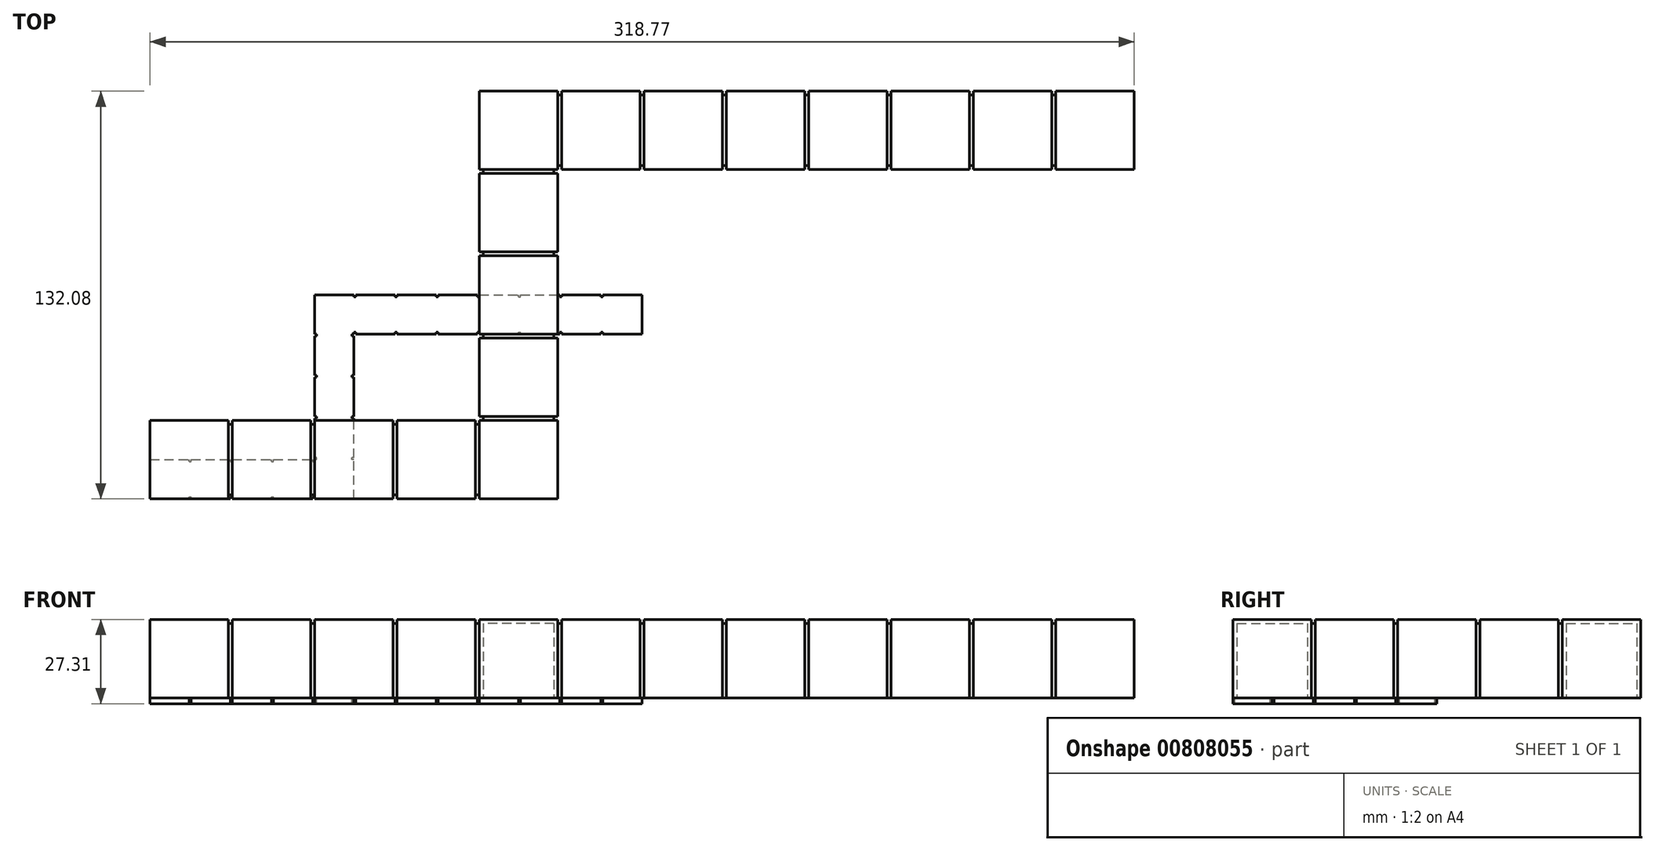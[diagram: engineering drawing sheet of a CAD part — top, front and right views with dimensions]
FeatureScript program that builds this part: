
annotation { "Feature Type Name" : "Feature", "Feature Type Description" : "" }
export const myFeature = defineFeature(function(context is Context, id is Id, definition is map)
    precondition{}
    {
        {
            var Q0;
            Q0=qCreatedBy(makeId("Top.planeOp"),FACE);
            var sketch = newSketch(context, id + "F0", { "sketchPlane" : qUnion([Q0])});
            skLineSegment(sketch, "E0.bottom", {"start": v(0, 0) * mm, "end": v(25.4, 0) * mm});
            skLineSegment(sketch, "E0.top", {"start": v(0, 25.4) * mm, "end": v(25.4, 25.4) * mm});
            skLineSegment(sketch, "E0.left", {"start": v(0, 0) * mm, "end": v(0, 25.4) * mm});
            skLineSegment(sketch, "E0.right", {"start": v(25.4, 0) * mm, "end": v(25.4, 25.4) * mm});
            skLineSegment(sketch, "E1.bottom", {"start": v(25.4, 24.13) * mm, "end": v(26.67, 24.13) * mm});
            skLineSegment(sketch, "E1.top", {"start": v(25.4, 1.27) * mm, "end": v(26.67, 1.27) * mm});
            skLineSegment(sketch, "E1.left", {"start": v(25.4, 24.13) * mm, "end": v(25.4, 1.27) * mm});
            skLineSegment(sketch, "E1.right", {"start": v(26.67, 24.13) * mm, "end": v(26.67, 1.27) * mm});
            skLineSegment(sketch, "E2", {"start": v(25.4, 25.4) * mm, "end": v(25.4, 24.13) * mm});
            skLineSegment(sketch, "E3", {"start": v(25.4, 0) * mm, "end": v(25.4, 1.27) * mm});
            skLineSegment(sketch, "E4.bottom", {"start": v(26.67, 0) * mm, "end": v(52.07, 0) * mm});
            skLineSegment(sketch, "E4.top", {"start": v(26.67, 25.4) * mm, "end": v(52.07, 25.4) * mm});
            skLineSegment(sketch, "E4.left", {"start": v(26.67, 0) * mm, "end": v(26.67, 25.4) * mm});
            skLineSegment(sketch, "E4.right", {"start": v(52.07, 0) * mm, "end": v(52.07, 25.4) * mm});
            skLineSegment(sketch, "E5.bottom", {"start": v(52.07, 24.13) * mm, "end": v(53.34, 24.13) * mm});
            skLineSegment(sketch, "E5.top", {"start": v(52.07, 1.27) * mm, "end": v(53.34, 1.27) * mm});
            skLineSegment(sketch, "E5.left", {"start": v(52.07, 24.13) * mm, "end": v(52.07, 1.27) * mm});
            skLineSegment(sketch, "E5.right", {"start": v(53.34, 24.13) * mm, "end": v(53.34, 1.27) * mm});
            skLineSegment(sketch, "E6", {"start": v(52.07, 25.4) * mm, "end": v(52.07, 24.13) * mm});
            skLineSegment(sketch, "E7", {"start": v(52.07, 0) * mm, "end": v(52.07, 1.27) * mm});
            skLineSegment(sketch, "E8.bottom", {"start": v(53.34, 0) * mm, "end": v(78.74, 0) * mm});
            skLineSegment(sketch, "E8.top", {"start": v(53.34, 25.4) * mm, "end": v(78.74, 25.4) * mm});
            skLineSegment(sketch, "E8.left", {"start": v(53.34, 0) * mm, "end": v(53.34, 25.4) * mm});
            skLineSegment(sketch, "E8.right", {"start": v(78.74, 0) * mm, "end": v(78.74, 25.4) * mm});
            skLineSegment(sketch, "E9.bottom", {"start": v(78.74, 24.13) * mm, "end": v(80, 24.13) * mm});
            skLineSegment(sketch, "E9.top", {"start": v(78.74, 1.27) * mm, "end": v(80, 1.27) * mm});
            skLineSegment(sketch, "E9.left", {"start": v(78.74, 24.13) * mm, "end": v(78.74, 1.27) * mm});
            skLineSegment(sketch, "E9.right", {"start": v(80, 24.13) * mm, "end": v(80, 1.27) * mm});
            skLineSegment(sketch, "E10", {"start": v(78.74, 25.4) * mm, "end": v(78.74, 24.13) * mm});
            skLineSegment(sketch, "E11", {"start": v(78.74, 0) * mm, "end": v(78.74, 1.27) * mm});
            skLineSegment(sketch, "E12.bottom", {"start": v(80, 0) * mm, "end": v(105.4, 0) * mm});
            skLineSegment(sketch, "E12.top", {"start": v(80, 25.4) * mm, "end": v(105.4, 25.4) * mm});
            skLineSegment(sketch, "E12.left", {"start": v(80, 0) * mm, "end": v(80, 25.4) * mm});
            skLineSegment(sketch, "E12.right", {"start": v(105.4, 0) * mm, "end": v(105.4, 25.4) * mm});
            skLineSegment(sketch, "E13.bottom", {"start": v(105.4, 24.13) * mm, "end": v(106.68, 24.13) * mm});
            skLineSegment(sketch, "E13.top", {"start": v(105.4, 1.27) * mm, "end": v(106.68, 1.27) * mm});
            skLineSegment(sketch, "E13.left", {"start": v(105.4, 24.13) * mm, "end": v(105.4, 1.27) * mm});
            skLineSegment(sketch, "E13.right", {"start": v(106.68, 24.13) * mm, "end": v(106.68, 1.27) * mm});
            skLineSegment(sketch, "E14", {"start": v(105.4, 25.4) * mm, "end": v(105.4, 24.13) * mm});
            skLineSegment(sketch, "E15", {"start": v(105.4, 0) * mm, "end": v(105.4, 1.27) * mm});
            skLineSegment(sketch, "E16.bottom", {"start": v(132.08, 0) * mm, "end": v(132.08, 25.4) * mm});
            skLineSegment(sketch, "E16.top", {"start": v(106.68, 0) * mm, "end": v(106.68, 25.4) * mm});
            skLineSegment(sketch, "E16.left", {"start": v(132.08, 0) * mm, "end": v(106.68, 0) * mm});
            skLineSegment(sketch, "E16.right", {"start": v(132.08, 25.4) * mm, "end": v(106.68, 25.4) * mm});
            skLineSegment(sketch, "E17.bottom", {"start": v(107.95, 25.4) * mm, "end": v(107.95, 26.67) * mm});
            skLineSegment(sketch, "E17.top", {"start": v(130.8, 25.4) * mm, "end": v(130.8, 26.67) * mm});
            skLineSegment(sketch, "E17.left", {"start": v(107.95, 25.4) * mm, "end": v(130.8, 25.4) * mm});
            skLineSegment(sketch, "E17.right", {"start": v(107.95, 26.67) * mm, "end": v(130.8, 26.67) * mm});
            skLineSegment(sketch, "E18", {"start": v(106.68, 25.4) * mm, "end": v(107.95, 25.4) * mm});
            skLineSegment(sketch, "E19", {"start": v(132.08, 25.4) * mm, "end": v(130.8, 25.4) * mm});
            skLineSegment(sketch, "E20.bottom", {"start": v(132.08, 26.67) * mm, "end": v(132.08, 52.07) * mm});
            skLineSegment(sketch, "E20.top", {"start": v(106.68, 26.67) * mm, "end": v(106.68, 52.07) * mm});
            skLineSegment(sketch, "E20.left", {"start": v(132.08, 26.67) * mm, "end": v(106.68, 26.67) * mm});
            skLineSegment(sketch, "E20.right", {"start": v(132.08, 52.07) * mm, "end": v(106.68, 52.07) * mm});
            skLineSegment(sketch, "E21.bottom", {"start": v(107.95, 52.07) * mm, "end": v(107.95, 53.34) * mm});
            skLineSegment(sketch, "E21.top", {"start": v(130.8, 52.07) * mm, "end": v(130.8, 53.34) * mm});
            skLineSegment(sketch, "E21.left", {"start": v(107.95, 52.07) * mm, "end": v(130.8, 52.07) * mm});
            skLineSegment(sketch, "E21.right", {"start": v(107.95, 53.34) * mm, "end": v(130.8, 53.34) * mm});
            skLineSegment(sketch, "E22", {"start": v(106.68, 52.07) * mm, "end": v(107.95, 52.07) * mm});
            skLineSegment(sketch, "E23", {"start": v(132.08, 52.07) * mm, "end": v(130.8, 52.07) * mm});
            skLineSegment(sketch, "E24.bottom", {"start": v(132.08, 53.34) * mm, "end": v(132.08, 78.74) * mm});
            skLineSegment(sketch, "E24.top", {"start": v(106.68, 53.34) * mm, "end": v(106.68, 78.74) * mm});
            skLineSegment(sketch, "E24.left", {"start": v(132.08, 53.34) * mm, "end": v(106.68, 53.34) * mm});
            skLineSegment(sketch, "E24.right", {"start": v(132.08, 78.74) * mm, "end": v(106.68, 78.74) * mm});
            skLineSegment(sketch, "E25.bottom", {"start": v(107.95, 78.74) * mm, "end": v(107.95, 80) * mm});
            skLineSegment(sketch, "E25.top", {"start": v(130.8, 78.74) * mm, "end": v(130.8, 80) * mm});
            skLineSegment(sketch, "E25.left", {"start": v(107.95, 78.74) * mm, "end": v(130.8, 78.74) * mm});
            skLineSegment(sketch, "E25.right", {"start": v(107.95, 80) * mm, "end": v(130.8, 80) * mm});
            skLineSegment(sketch, "E26", {"start": v(106.68, 78.74) * mm, "end": v(107.95, 78.74) * mm});
            skLineSegment(sketch, "E27", {"start": v(132.08, 78.74) * mm, "end": v(130.8, 78.74) * mm});
            skLineSegment(sketch, "E28.bottom", {"start": v(132.08, 80) * mm, "end": v(132.08, 105.4) * mm});
            skLineSegment(sketch, "E28.top", {"start": v(106.68, 80) * mm, "end": v(106.68, 105.4) * mm});
            skLineSegment(sketch, "E28.left", {"start": v(132.08, 80) * mm, "end": v(106.68, 80) * mm});
            skLineSegment(sketch, "E28.right", {"start": v(132.08, 105.4) * mm, "end": v(106.68, 105.4) * mm});
            skLineSegment(sketch, "E29.bottom", {"start": v(107.95, 105.4) * mm, "end": v(107.95, 106.68) * mm});
            skLineSegment(sketch, "E29.top", {"start": v(130.8, 105.4) * mm, "end": v(130.8, 106.68) * mm});
            skLineSegment(sketch, "E29.left", {"start": v(107.95, 105.4) * mm, "end": v(130.8, 105.4) * mm});
            skLineSegment(sketch, "E29.right", {"start": v(107.95, 106.68) * mm, "end": v(130.8, 106.68) * mm});
            skLineSegment(sketch, "E30", {"start": v(106.68, 105.4) * mm, "end": v(107.95, 105.4) * mm});
            skLineSegment(sketch, "E31", {"start": v(132.08, 105.4) * mm, "end": v(130.8, 105.4) * mm});
            skLineSegment(sketch, "E32", {"start": v(106.68, 1.27) * mm, "end": v(106.68, 12.7) * mm});
            skLineSegment(sketch, "E33", {"start": v(106.68, 12.7) * mm, "end": v(105.4, 12.7) * mm});
            skLineSegment(sketch, "E34.bottom", {"start": v(106.68, 106.68) * mm, "end": v(132.08, 106.68) * mm});
            skLineSegment(sketch, "E34.top", {"start": v(106.68, 132.08) * mm, "end": v(132.08, 132.08) * mm});
            skLineSegment(sketch, "E34.left", {"start": v(106.68, 106.68) * mm, "end": v(106.68, 132.08) * mm});
            skLineSegment(sketch, "E34.right", {"start": v(132.08, 106.68) * mm, "end": v(132.08, 132.08) * mm});
            skLineSegment(sketch, "E35.bottom", {"start": v(132.08, 130.8) * mm, "end": v(133.35, 130.8) * mm});
            skLineSegment(sketch, "E35.top", {"start": v(132.08, 107.95) * mm, "end": v(133.35, 107.95) * mm});
            skLineSegment(sketch, "E35.left", {"start": v(132.08, 130.8) * mm, "end": v(132.08, 107.95) * mm});
            skLineSegment(sketch, "E35.right", {"start": v(133.35, 130.8) * mm, "end": v(133.35, 107.95) * mm});
            skLineSegment(sketch, "E36", {"start": v(132.08, 132.08) * mm, "end": v(132.08, 130.8) * mm});
            skLineSegment(sketch, "E37", {"start": v(132.08, 106.68) * mm, "end": v(132.08, 107.95) * mm});
            skLineSegment(sketch, "E38.bottom", {"start": v(133.35, 106.68) * mm, "end": v(158.75, 106.68) * mm});
            skLineSegment(sketch, "E38.top", {"start": v(133.35, 132.08) * mm, "end": v(158.75, 132.08) * mm});
            skLineSegment(sketch, "E38.left", {"start": v(133.35, 106.68) * mm, "end": v(133.35, 132.08) * mm});
            skLineSegment(sketch, "E38.right", {"start": v(158.75, 106.68) * mm, "end": v(158.75, 132.08) * mm});
            skLineSegment(sketch, "E39.bottom", {"start": v(158.75, 130.8) * mm, "end": v(160.02, 130.8) * mm});
            skLineSegment(sketch, "E39.top", {"start": v(158.75, 107.95) * mm, "end": v(160.02, 107.95) * mm});
            skLineSegment(sketch, "E39.left", {"start": v(158.75, 130.8) * mm, "end": v(158.75, 107.95) * mm});
            skLineSegment(sketch, "E39.right", {"start": v(160.02, 130.8) * mm, "end": v(160.02, 107.95) * mm});
            skLineSegment(sketch, "E40", {"start": v(158.75, 132.08) * mm, "end": v(158.75, 130.8) * mm});
            skLineSegment(sketch, "E41", {"start": v(158.75, 106.68) * mm, "end": v(158.75, 107.95) * mm});
            skLineSegment(sketch, "E42.bottom", {"start": v(160.02, 106.68) * mm, "end": v(185.42, 106.68) * mm});
            skLineSegment(sketch, "E42.top", {"start": v(160.02, 132.08) * mm, "end": v(185.42, 132.08) * mm});
            skLineSegment(sketch, "E42.left", {"start": v(160.02, 106.68) * mm, "end": v(160.02, 132.08) * mm});
            skLineSegment(sketch, "E42.right", {"start": v(185.42, 106.68) * mm, "end": v(185.42, 132.08) * mm});
            skLineSegment(sketch, "E43.bottom", {"start": v(185.42, 130.8) * mm, "end": v(186.7, 130.8) * mm});
            skLineSegment(sketch, "E43.top", {"start": v(185.42, 107.95) * mm, "end": v(186.7, 107.95) * mm});
            skLineSegment(sketch, "E43.left", {"start": v(185.42, 130.8) * mm, "end": v(185.42, 107.95) * mm});
            skLineSegment(sketch, "E43.right", {"start": v(186.7, 130.8) * mm, "end": v(186.7, 107.95) * mm});
            skLineSegment(sketch, "E44", {"start": v(185.42, 132.08) * mm, "end": v(185.42, 130.8) * mm});
            skLineSegment(sketch, "E45", {"start": v(185.42, 106.68) * mm, "end": v(185.42, 107.95) * mm});
            skLineSegment(sketch, "E46.bottom", {"start": v(186.7, 106.68) * mm, "end": v(212.1, 106.68) * mm});
            skLineSegment(sketch, "E46.top", {"start": v(186.7, 132.08) * mm, "end": v(212.1, 132.08) * mm});
            skLineSegment(sketch, "E46.left", {"start": v(186.7, 106.68) * mm, "end": v(186.7, 132.08) * mm});
            skLineSegment(sketch, "E46.right", {"start": v(212.1, 106.68) * mm, "end": v(212.1, 132.08) * mm});
            skLineSegment(sketch, "E47.bottom", {"start": v(212.1, 130.8) * mm, "end": v(213.36, 130.8) * mm});
            skLineSegment(sketch, "E47.top", {"start": v(212.1, 107.95) * mm, "end": v(213.36, 107.95) * mm});
            skLineSegment(sketch, "E47.left", {"start": v(212.1, 130.8) * mm, "end": v(212.1, 107.95) * mm});
            skLineSegment(sketch, "E47.right", {"start": v(213.36, 130.8) * mm, "end": v(213.36, 107.95) * mm});
            skLineSegment(sketch, "E48", {"start": v(212.1, 132.08) * mm, "end": v(212.1, 130.8) * mm});
            skLineSegment(sketch, "E49", {"start": v(212.1, 106.68) * mm, "end": v(212.1, 107.95) * mm});
            skLineSegment(sketch, "E50.bottom", {"start": v(213.36, 106.68) * mm, "end": v(238.76, 106.68) * mm});
            skLineSegment(sketch, "E50.top", {"start": v(213.36, 132.08) * mm, "end": v(238.76, 132.08) * mm});
            skLineSegment(sketch, "E50.left", {"start": v(213.36, 106.68) * mm, "end": v(213.36, 132.08) * mm});
            skLineSegment(sketch, "E50.right", {"start": v(238.76, 106.68) * mm, "end": v(238.76, 132.08) * mm});
            skLineSegment(sketch, "E51.bottom", {"start": v(238.76, 130.8) * mm, "end": v(240.03, 130.8) * mm});
            skLineSegment(sketch, "E51.top", {"start": v(238.76, 107.95) * mm, "end": v(240.03, 107.95) * mm});
            skLineSegment(sketch, "E51.left", {"start": v(238.76, 130.8) * mm, "end": v(238.76, 107.95) * mm});
            skLineSegment(sketch, "E51.right", {"start": v(240.03, 130.8) * mm, "end": v(240.03, 107.95) * mm});
            skLineSegment(sketch, "E52", {"start": v(238.76, 132.08) * mm, "end": v(238.76, 130.8) * mm});
            skLineSegment(sketch, "E53", {"start": v(238.76, 106.68) * mm, "end": v(238.76, 107.95) * mm});
            skLineSegment(sketch, "E54.bottom", {"start": v(240.03, 106.68) * mm, "end": v(265.43, 106.68) * mm});
            skLineSegment(sketch, "E54.top", {"start": v(240.03, 132.08) * mm, "end": v(265.43, 132.08) * mm});
            skLineSegment(sketch, "E54.left", {"start": v(240.03, 106.68) * mm, "end": v(240.03, 132.08) * mm});
            skLineSegment(sketch, "E54.right", {"start": v(265.43, 106.68) * mm, "end": v(265.43, 132.08) * mm});
            skLineSegment(sketch, "E55.bottom", {"start": v(265.43, 130.8) * mm, "end": v(266.7, 130.8) * mm});
            skLineSegment(sketch, "E55.top", {"start": v(265.43, 107.95) * mm, "end": v(266.7, 107.95) * mm});
            skLineSegment(sketch, "E55.left", {"start": v(265.43, 130.8) * mm, "end": v(265.43, 107.95) * mm});
            skLineSegment(sketch, "E55.right", {"start": v(266.7, 130.8) * mm, "end": v(266.7, 107.95) * mm});
            skLineSegment(sketch, "E56", {"start": v(265.43, 132.08) * mm, "end": v(265.43, 130.8) * mm});
            skLineSegment(sketch, "E57", {"start": v(265.43, 106.68) * mm, "end": v(265.43, 107.95) * mm});
            skLineSegment(sketch, "E58.bottom", {"start": v(266.7, 106.68) * mm, "end": v(292.1, 106.68) * mm});
            skLineSegment(sketch, "E58.top", {"start": v(266.7, 132.08) * mm, "end": v(292.1, 132.08) * mm});
            skLineSegment(sketch, "E58.left", {"start": v(266.7, 106.68) * mm, "end": v(266.7, 132.08) * mm});
            skLineSegment(sketch, "E58.right", {"start": v(292.1, 106.68) * mm, "end": v(292.1, 132.08) * mm});
            skLineSegment(sketch, "E59.bottom", {"start": v(292.1, 130.8) * mm, "end": v(293.37, 130.8) * mm});
            skLineSegment(sketch, "E59.top", {"start": v(292.1, 107.95) * mm, "end": v(293.37, 107.95) * mm});
            skLineSegment(sketch, "E59.left", {"start": v(292.1, 130.8) * mm, "end": v(292.1, 107.95) * mm});
            skLineSegment(sketch, "E59.right", {"start": v(293.37, 130.8) * mm, "end": v(293.37, 107.95) * mm});
            skLineSegment(sketch, "E60", {"start": v(292.1, 132.08) * mm, "end": v(292.1, 130.8) * mm});
            skLineSegment(sketch, "E61", {"start": v(292.1, 106.68) * mm, "end": v(292.1, 107.95) * mm});
            skLineSegment(sketch, "E62.bottom", {"start": v(293.37, 106.68) * mm, "end": v(318.77, 106.68) * mm});
            skLineSegment(sketch, "E62.top", {"start": v(293.37, 132.08) * mm, "end": v(318.77, 132.08) * mm});
            skLineSegment(sketch, "E62.left", {"start": v(293.37, 106.68) * mm, "end": v(293.37, 132.08) * mm});
            skLineSegment(sketch, "E62.right", {"start": v(318.77, 106.68) * mm, "end": v(318.77, 132.08) * mm});
            skLineSegment(sketch, "E63.left", {"start": v(318.77, 130.8) * mm, "end": v(318.77, 107.95) * mm});
            skLineSegment(sketch, "E64", {"start": v(318.77, 132.08) * mm, "end": v(318.77, 130.8) * mm});
            skLineSegment(sketch, "E65", {"start": v(318.77, 106.68) * mm, "end": v(318.77, 107.95) * mm});
            skSolve(sketch);
        }
        {
            var Q0;
            {var subQ0=sQuery(id+"F0.wireOp",EDGE,"E1.bottom");Q0=makeQuery(id+"F0.imprint","IMPRINT",FACE,{"disambiguationData":[TD([[makeQuery(id+"F0.imprint","IMPRINT",EDGE,{"derivedFrom":subQ0}),-1.0]])]});}
            var Q1;
            {var subQ0=sQuery(id+"F0.wireOp",EDGE,"E5.bottom");Q1=makeQuery(id+"F0.imprint","IMPRINT",FACE,{"disambiguationData":[TD([[makeQuery(id+"F0.imprint","IMPRINT",EDGE,{"derivedFrom":subQ0}),-1.0]])]});}
            var Q2;
            {var subQ0=sQuery(id+"F0.wireOp",EDGE,"E9.bottom");Q2=makeQuery(id+"F0.imprint","IMPRINT",FACE,{"disambiguationData":[TD([[makeQuery(id+"F0.imprint","IMPRINT",EDGE,{"derivedFrom":subQ0}),-1.0]])]});}
            var Q3;
            {var subQ0=sQuery(id+"F0.wireOp",EDGE,"E13.top");Q3=makeQuery(id+"F0.imprint","IMPRINT",FACE,{"disambiguationData":[TD([[makeQuery(id+"F0.imprint","IMPRINT",EDGE,{"derivedFrom":subQ0}),1.0]])]});}
            var Q4;
            {var subQ0=sQuery(id+"F0.wireOp",EDGE,"E13.bottom");Q4=makeQuery(id+"F0.imprint","IMPRINT",FACE,{"disambiguationData":[TD([[makeQuery(id+"F0.imprint","IMPRINT",EDGE,{"derivedFrom":subQ0}),-1.0]])]});}
            var Q5;
            {var subQ0=sQuery(id+"F0.wireOp",EDGE,"E17.bottom");Q5=makeQuery(id+"F0.imprint","IMPRINT",FACE,{"disambiguationData":[TD([[makeQuery(id+"F0.imprint","IMPRINT",EDGE,{"derivedFrom":subQ0}),-1.0]])]});}
            var Q6;
            {var subQ0=sQuery(id+"F0.wireOp",EDGE,"E21.bottom");Q6=makeQuery(id+"F0.imprint","IMPRINT",FACE,{"disambiguationData":[TD([[makeQuery(id+"F0.imprint","IMPRINT",EDGE,{"derivedFrom":subQ0}),-1.0]])]});}
            var Q7;
            {var subQ0=sQuery(id+"F0.wireOp",EDGE,"E25.bottom");Q7=makeQuery(id+"F0.imprint","IMPRINT",FACE,{"disambiguationData":[TD([[makeQuery(id+"F0.imprint","IMPRINT",EDGE,{"derivedFrom":subQ0}),-1.0]])]});}
            var Q8;
            {var subQ0=sQuery(id+"F0.wireOp",EDGE,"E29.bottom");Q8=makeQuery(id+"F0.imprint","IMPRINT",FACE,{"disambiguationData":[TD([[makeQuery(id+"F0.imprint","IMPRINT",EDGE,{"derivedFrom":subQ0}),-1.0]])]});}
            var Q9;
            {var subQ0=sQuery(id+"F0.wireOp",EDGE,"E35.bottom");Q9=makeQuery(id+"F0.imprint","IMPRINT",FACE,{"disambiguationData":[TD([[makeQuery(id+"F0.imprint","IMPRINT",EDGE,{"derivedFrom":subQ0}),-1.0]])]});}
            var Q10;
            {var subQ0=sQuery(id+"F0.wireOp",EDGE,"E39.bottom");Q10=makeQuery(id+"F0.imprint","IMPRINT",FACE,{"disambiguationData":[TD([[makeQuery(id+"F0.imprint","IMPRINT",EDGE,{"derivedFrom":subQ0}),-1.0]])]});}
            var Q11;
            {var subQ0=sQuery(id+"F0.wireOp",EDGE,"E43.bottom");Q11=makeQuery(id+"F0.imprint","IMPRINT",FACE,{"disambiguationData":[TD([[makeQuery(id+"F0.imprint","IMPRINT",EDGE,{"derivedFrom":subQ0}),-1.0]])]});}
            var Q12;
            {var subQ0=sQuery(id+"F0.wireOp",EDGE,"E47.bottom");Q12=makeQuery(id+"F0.imprint","IMPRINT",FACE,{"disambiguationData":[TD([[makeQuery(id+"F0.imprint","IMPRINT",EDGE,{"derivedFrom":subQ0}),-1.0]])]});}
            var Q13;
            {var subQ0=sQuery(id+"F0.wireOp",EDGE,"E51.bottom");Q13=makeQuery(id+"F0.imprint","IMPRINT",FACE,{"disambiguationData":[TD([[makeQuery(id+"F0.imprint","IMPRINT",EDGE,{"derivedFrom":subQ0}),-1.0]])]});}
            var Q14;
            {var subQ0=sQuery(id+"F0.wireOp",EDGE,"E55.bottom");Q14=makeQuery(id+"F0.imprint","IMPRINT",FACE,{"disambiguationData":[TD([[makeQuery(id+"F0.imprint","IMPRINT",EDGE,{"derivedFrom":subQ0}),-1.0]])]});}
            var Q15;
            {var subQ0=sQuery(id+"F0.wireOp",EDGE,"E59.bottom");Q15=makeQuery(id+"F0.imprint","IMPRINT",FACE,{"disambiguationData":[TD([[makeQuery(id+"F0.imprint","IMPRINT",EDGE,{"derivedFrom":subQ0}),-1.0]])]});}
            extrude(context, id + "F1", {"entities" : qUnion([Q0, Q1, Q2, Q3, Q4, Q5, Q6, Q7, Q8, Q9, Q10, Q11, Q12, Q13, Q14, Q15]), "depth" : 24.13 * mm, "offsetDistance" : 25.4 * mm});
        }
        {
            var Q0;
            Q0=makeQuery(id+"F0.imprint","IMPRINT",FACE,{"disambiguationData":[TD([[makeQuery(id+"F0.imprint","IMPRINT",EDGE,{"derivedFrom":sQuery(id+"F0.wireOp",EDGE,"E0.bottom")}),1.0]])]});
            var Q1;
            {var subQ3=sQuery(id+"F0.wireOp",EDGE,"E4.bottom");Q1=makeQuery(id+"F0.imprint","IMPRINT",FACE,{"disambiguationData":[TD([[makeQuery(id+"F0.imprint","IMPRINT",EDGE,{"derivedFrom":subQ3}),1.0]])]});}
            var Q2;
            {var subQ3=sQuery(id+"F0.wireOp",EDGE,"E8.bottom");Q2=makeQuery(id+"F0.imprint","IMPRINT",FACE,{"disambiguationData":[TD([[makeQuery(id+"F0.imprint","IMPRINT",EDGE,{"derivedFrom":subQ3}),1.0]])]});}
            var Q3;
            {var subQ3=sQuery(id+"F0.wireOp",EDGE,"E12.bottom");Q3=makeQuery(id+"F0.imprint","IMPRINT",FACE,{"disambiguationData":[TD([[makeQuery(id+"F0.imprint","IMPRINT",EDGE,{"derivedFrom":subQ3}),1.0]])]});}
            var Q4;
            Q4=makeQuery(id+"F0.imprint","IMPRINT",FACE,{"disambiguationData":[TD([[makeQuery(id+"F0.imprint","IMPRINT",EDGE,{"derivedFrom":sQuery(id+"F0.wireOp",EDGE,"E16.bottom")}),1.0]])]});
            var Q5;
            {var subQ3=sQuery(id+"F0.wireOp",EDGE,"E20.bottom");Q5=makeQuery(id+"F0.imprint","IMPRINT",FACE,{"disambiguationData":[TD([[makeQuery(id+"F0.imprint","IMPRINT",EDGE,{"derivedFrom":subQ3}),1.0]])]});}
            var Q6;
            {var subQ3=sQuery(id+"F0.wireOp",EDGE,"E24.bottom");Q6=makeQuery(id+"F0.imprint","IMPRINT",FACE,{"disambiguationData":[TD([[makeQuery(id+"F0.imprint","IMPRINT",EDGE,{"derivedFrom":subQ3}),1.0]])]});}
            var Q7;
            {var subQ3=sQuery(id+"F0.wireOp",EDGE,"E28.bottom");Q7=makeQuery(id+"F0.imprint","IMPRINT",FACE,{"disambiguationData":[TD([[makeQuery(id+"F0.imprint","IMPRINT",EDGE,{"derivedFrom":subQ3}),1.0]])]});}
            var Q8;
            Q8=makeQuery(id+"F0.imprint","IMPRINT",FACE,{"disambiguationData":[TD([[makeQuery(id+"F0.imprint","IMPRINT",EDGE,{"derivedFrom":sQuery(id+"F0.wireOp",EDGE,"E34.top")}),-1.0]])]});
            var Q9;
            {var subQ3=sQuery(id+"F0.wireOp",EDGE,"E38.bottom");Q9=makeQuery(id+"F0.imprint","IMPRINT",FACE,{"disambiguationData":[TD([[makeQuery(id+"F0.imprint","IMPRINT",EDGE,{"derivedFrom":subQ3}),1.0]])]});}
            var Q10;
            {var subQ3=sQuery(id+"F0.wireOp",EDGE,"E42.bottom");Q10=makeQuery(id+"F0.imprint","IMPRINT",FACE,{"disambiguationData":[TD([[makeQuery(id+"F0.imprint","IMPRINT",EDGE,{"derivedFrom":subQ3}),1.0]])]});}
            var Q11;
            {var subQ3=sQuery(id+"F0.wireOp",EDGE,"E46.bottom");Q11=makeQuery(id+"F0.imprint","IMPRINT",FACE,{"disambiguationData":[TD([[makeQuery(id+"F0.imprint","IMPRINT",EDGE,{"derivedFrom":subQ3}),1.0]])]});}
            var Q12;
            {var subQ3=sQuery(id+"F0.wireOp",EDGE,"E50.bottom");Q12=makeQuery(id+"F0.imprint","IMPRINT",FACE,{"disambiguationData":[TD([[makeQuery(id+"F0.imprint","IMPRINT",EDGE,{"derivedFrom":subQ3}),1.0]])]});}
            var Q13;
            {var subQ3=sQuery(id+"F0.wireOp",EDGE,"E54.bottom");Q13=makeQuery(id+"F0.imprint","IMPRINT",FACE,{"disambiguationData":[TD([[makeQuery(id+"F0.imprint","IMPRINT",EDGE,{"derivedFrom":subQ3}),1.0]])]});}
            var Q14;
            {var subQ3=sQuery(id+"F0.wireOp",EDGE,"E58.bottom");Q14=makeQuery(id+"F0.imprint","IMPRINT",FACE,{"disambiguationData":[TD([[makeQuery(id+"F0.imprint","IMPRINT",EDGE,{"derivedFrom":subQ3}),1.0]])]});}
            var Q15;
            {var subQ3=sQuery(id+"F0.wireOp",EDGE,"E62.bottom");Q15=makeQuery(id+"F0.imprint","IMPRINT",FACE,{"disambiguationData":[TD([[makeQuery(id+"F0.imprint","IMPRINT",EDGE,{"derivedFrom":subQ3}),1.0]])]});}
            extrude(context, id + "F2", {"entities" : qUnion([Q0, Q1, Q2, Q3, Q4, Q5, Q6, Q7, Q8, Q9, Q10, Q11, Q12, Q13, Q14, Q15]), "depth" : 25.4 * mm, "offsetDistance" : 25.4 * mm});
        }
        {
            var Q0;
            {var subQ3=sQuery(id+"F0.wireOp",EDGE,"E8.bottom");Q0=makeQuery(id+"F0.imprint","IMPRINT",FACE,{"disambiguationData":[TD([[makeQuery(id+"F0.imprint","IMPRINT",EDGE,{"derivedFrom":subQ3}),1.0]])]});}
            var Q1;
            {var subQ3=sQuery(id+"F0.wireOp",EDGE,"E50.bottom");Q1=makeQuery(id+"F0.imprint","IMPRINT",FACE,{"disambiguationData":[TD([[makeQuery(id+"F0.imprint","IMPRINT",EDGE,{"derivedFrom":subQ3}),1.0]])]});}
            var Q2;
            Q2=makeQuery(id+"F0.imprint","IMPRINT",FACE,{"disambiguationData":[TD([[makeQuery(id+"F0.imprint","IMPRINT",EDGE,{"derivedFrom":sQuery(id+"F0.wireOp",EDGE,"E34.top")}),-1.0]])]});
            var Q3;
            Q3=makeQuery(id+"F0.imprint","IMPRINT",FACE,{"disambiguationData":[TD([[makeQuery(id+"F0.imprint","IMPRINT",EDGE,{"derivedFrom":sQuery(id+"F0.wireOp",EDGE,"E0.bottom")}),1.0]])]});
            var Q4;
            {var subQ3=sQuery(id+"F0.wireOp",EDGE,"E62.bottom");Q4=makeQuery(id+"F0.imprint","IMPRINT",FACE,{"disambiguationData":[TD([[makeQuery(id+"F0.imprint","IMPRINT",EDGE,{"derivedFrom":subQ3}),1.0]])]});}
            var Q5;
            {var subQ3=sQuery(id+"F0.wireOp",EDGE,"E28.bottom");Q5=makeQuery(id+"F0.imprint","IMPRINT",FACE,{"disambiguationData":[TD([[makeQuery(id+"F0.imprint","IMPRINT",EDGE,{"derivedFrom":subQ3}),1.0]])]});}
            var Q6;
            {var subQ3=sQuery(id+"F0.wireOp",EDGE,"E24.bottom");Q6=makeQuery(id+"F0.imprint","IMPRINT",FACE,{"disambiguationData":[TD([[makeQuery(id+"F0.imprint","IMPRINT",EDGE,{"derivedFrom":subQ3}),1.0]])]});}
            var Q7;
            {var subQ3=sQuery(id+"F0.wireOp",EDGE,"E20.bottom");Q7=makeQuery(id+"F0.imprint","IMPRINT",FACE,{"disambiguationData":[TD([[makeQuery(id+"F0.imprint","IMPRINT",EDGE,{"derivedFrom":subQ3}),1.0]])]});}
            var Q8;
            {var subQ3=sQuery(id+"F0.wireOp",EDGE,"E4.bottom");Q8=makeQuery(id+"F0.imprint","IMPRINT",FACE,{"disambiguationData":[TD([[makeQuery(id+"F0.imprint","IMPRINT",EDGE,{"derivedFrom":subQ3}),1.0]])]});}
            var Q9;
            {var subQ3=sQuery(id+"F0.wireOp",EDGE,"E42.bottom");Q9=makeQuery(id+"F0.imprint","IMPRINT",FACE,{"disambiguationData":[TD([[makeQuery(id+"F0.imprint","IMPRINT",EDGE,{"derivedFrom":subQ3}),1.0]])]});}
            var Q10;
            {var subQ3=sQuery(id+"F0.wireOp",EDGE,"E46.bottom");Q10=makeQuery(id+"F0.imprint","IMPRINT",FACE,{"disambiguationData":[TD([[makeQuery(id+"F0.imprint","IMPRINT",EDGE,{"derivedFrom":subQ3}),1.0]])]});}
            var Q11;
            {var subQ3=sQuery(id+"F0.wireOp",EDGE,"E54.bottom");Q11=makeQuery(id+"F0.imprint","IMPRINT",FACE,{"disambiguationData":[TD([[makeQuery(id+"F0.imprint","IMPRINT",EDGE,{"derivedFrom":subQ3}),1.0]])]});}
            var Q12;
            Q12=makeQuery(id+"F0.imprint","IMPRINT",FACE,{"disambiguationData":[TD([[makeQuery(id+"F0.imprint","IMPRINT",EDGE,{"derivedFrom":sQuery(id+"F0.wireOp",EDGE,"E16.bottom")}),1.0]])]});
            var Q13;
            {var subQ3=sQuery(id+"F0.wireOp",EDGE,"E38.bottom");Q13=makeQuery(id+"F0.imprint","IMPRINT",FACE,{"disambiguationData":[TD([[makeQuery(id+"F0.imprint","IMPRINT",EDGE,{"derivedFrom":subQ3}),1.0]])]});}
            var Q14;
            {var subQ3=sQuery(id+"F0.wireOp",EDGE,"E12.bottom");Q14=makeQuery(id+"F0.imprint","IMPRINT",FACE,{"disambiguationData":[TD([[makeQuery(id+"F0.imprint","IMPRINT",EDGE,{"derivedFrom":subQ3}),1.0]])]});}
            var Q15;
            {var subQ3=sQuery(id+"F0.wireOp",EDGE,"E58.bottom");Q15=makeQuery(id+"F0.imprint","IMPRINT",FACE,{"disambiguationData":[TD([[makeQuery(id+"F0.imprint","IMPRINT",EDGE,{"derivedFrom":subQ3}),1.0]])]});}
            var Q16;
            {var subQ0=sQuery(id+"F0.wireOp",EDGE,"E35.bottom");Q16=makeQuery(id+"F0.imprint","IMPRINT",FACE,{"disambiguationData":[TD([[makeQuery(id+"F0.imprint","IMPRINT",EDGE,{"derivedFrom":subQ0}),-1.0]])]});}
            var Q17;
            {var subQ0=sQuery(id+"F0.wireOp",EDGE,"E29.bottom");Q17=makeQuery(id+"F0.imprint","IMPRINT",FACE,{"disambiguationData":[TD([[makeQuery(id+"F0.imprint","IMPRINT",EDGE,{"derivedFrom":subQ0}),-1.0]])]});}
            var Q18;
            {var subQ0=sQuery(id+"F0.wireOp",EDGE,"E51.bottom");Q18=makeQuery(id+"F0.imprint","IMPRINT",FACE,{"disambiguationData":[TD([[makeQuery(id+"F0.imprint","IMPRINT",EDGE,{"derivedFrom":subQ0}),-1.0]])]});}
            var Q19;
            {var subQ0=sQuery(id+"F0.wireOp",EDGE,"E43.bottom");Q19=makeQuery(id+"F0.imprint","IMPRINT",FACE,{"disambiguationData":[TD([[makeQuery(id+"F0.imprint","IMPRINT",EDGE,{"derivedFrom":subQ0}),-1.0]])]});}
            var Q20;
            {var subQ0=sQuery(id+"F0.wireOp",EDGE,"E39.bottom");Q20=makeQuery(id+"F0.imprint","IMPRINT",FACE,{"disambiguationData":[TD([[makeQuery(id+"F0.imprint","IMPRINT",EDGE,{"derivedFrom":subQ0}),-1.0]])]});}
            var Q21;
            {var subQ0=sQuery(id+"F0.wireOp",EDGE,"E5.bottom");Q21=makeQuery(id+"F0.imprint","IMPRINT",FACE,{"disambiguationData":[TD([[makeQuery(id+"F0.imprint","IMPRINT",EDGE,{"derivedFrom":subQ0}),-1.0]])]});}
            var Q22;
            {var subQ0=sQuery(id+"F0.wireOp",EDGE,"E47.bottom");Q22=makeQuery(id+"F0.imprint","IMPRINT",FACE,{"disambiguationData":[TD([[makeQuery(id+"F0.imprint","IMPRINT",EDGE,{"derivedFrom":subQ0}),-1.0]])]});}
            var Q23;
            {var subQ0=sQuery(id+"F0.wireOp",EDGE,"E25.bottom");Q23=makeQuery(id+"F0.imprint","IMPRINT",FACE,{"disambiguationData":[TD([[makeQuery(id+"F0.imprint","IMPRINT",EDGE,{"derivedFrom":subQ0}),-1.0]])]});}
            var Q24;
            {var subQ0=sQuery(id+"F0.wireOp",EDGE,"E21.bottom");Q24=makeQuery(id+"F0.imprint","IMPRINT",FACE,{"disambiguationData":[TD([[makeQuery(id+"F0.imprint","IMPRINT",EDGE,{"derivedFrom":subQ0}),-1.0]])]});}
            var Q25;
            {var subQ0=sQuery(id+"F0.wireOp",EDGE,"E17.bottom");Q25=makeQuery(id+"F0.imprint","IMPRINT",FACE,{"disambiguationData":[TD([[makeQuery(id+"F0.imprint","IMPRINT",EDGE,{"derivedFrom":subQ0}),-1.0]])]});}
            var Q26;
            {var subQ0=sQuery(id+"F0.wireOp",EDGE,"E9.bottom");Q26=makeQuery(id+"F0.imprint","IMPRINT",FACE,{"disambiguationData":[TD([[makeQuery(id+"F0.imprint","IMPRINT",EDGE,{"derivedFrom":subQ0}),-1.0]])]});}
            var Q27;
            {var subQ0=sQuery(id+"F0.wireOp",EDGE,"E1.bottom");Q27=makeQuery(id+"F0.imprint","IMPRINT",FACE,{"disambiguationData":[TD([[makeQuery(id+"F0.imprint","IMPRINT",EDGE,{"derivedFrom":subQ0}),-1.0]])]});}
            var Q28;
            {var subQ0=sQuery(id+"F0.wireOp",EDGE,"E55.bottom");Q28=makeQuery(id+"F0.imprint","IMPRINT",FACE,{"disambiguationData":[TD([[makeQuery(id+"F0.imprint","IMPRINT",EDGE,{"derivedFrom":subQ0}),-1.0]])]});}
            var Q29;
            {var subQ0=sQuery(id+"F0.wireOp",EDGE,"E13.top");Q29=makeQuery(id+"F0.imprint","IMPRINT",FACE,{"disambiguationData":[TD([[makeQuery(id+"F0.imprint","IMPRINT",EDGE,{"derivedFrom":subQ0}),1.0]])]});}
            var Q30;
            {var subQ0=sQuery(id+"F0.wireOp",EDGE,"E59.bottom");Q30=makeQuery(id+"F0.imprint","IMPRINT",FACE,{"disambiguationData":[TD([[makeQuery(id+"F0.imprint","IMPRINT",EDGE,{"derivedFrom":subQ0}),-1.0]])]});}
            var Q31;
            {var subQ0=sQuery(id+"F0.wireOp",EDGE,"E13.bottom");Q31=makeQuery(id+"F0.imprint","IMPRINT",FACE,{"disambiguationData":[TD([[makeQuery(id+"F0.imprint","IMPRINT",EDGE,{"derivedFrom":subQ0}),-1.0]])]});}
            extrude(context, id + "F3", {"entities" : qUnion([Q0, Q1, Q2, Q3, Q4, Q5, Q6, Q7, Q8, Q9, Q10, Q11, Q12, Q13, Q14, Q15, Q16, Q17, Q18, Q19, Q20, Q21, Q22, Q23, Q24, Q25, Q26, Q27, Q28, Q29, Q30, Q31]), "oppositeDirection" : true, "depth" : 3.8 * mm, "offsetDistance" : 25.4 * mm});
        }
        {
            var Q0;
            Q0=makeQuery(id+"F3.opExtrude","SWEPT_BODY",BODY,{"disambiguationData":[OSD([sQuery(id+"F0.wireOp",EDGE,"E0.bottom"),sQuery(id+"F0.wireOp",EDGE,"E0.top"),sQuery(id+"F0.wireOp",EDGE,"E0.left"),sQuery(id+"F0.wireOp",EDGE,"E1.bottom"),sQuery(id+"F0.wireOp",EDGE,"E1.top"),sQuery(id+"F0.wireOp",EDGE,"E2"),sQuery(id+"F0.wireOp",EDGE,"E3"),sQuery(id+"F0.wireOp",EDGE,"E4.bottom"),sQuery(id+"F0.wireOp",EDGE,"E4.top"),sQuery(id+"F0.wireOp",EDGE,"E4.left"),sQuery(id+"F0.wireOp",EDGE,"E5.bottom"),sQuery(id+"F0.wireOp",EDGE,"E5.top"),sQuery(id+"F0.wireOp",EDGE,"E6"),sQuery(id+"F0.wireOp",EDGE,"E7"),sQuery(id+"F0.wireOp",EDGE,"E8.bottom"),sQuery(id+"F0.wireOp",EDGE,"E8.top"),sQuery(id+"F0.wireOp",EDGE,"E8.left"),sQuery(id+"F0.wireOp",EDGE,"E9.bottom"),sQuery(id+"F0.wireOp",EDGE,"E9.top"),sQuery(id+"F0.wireOp",EDGE,"E10"),sQuery(id+"F0.wireOp",EDGE,"E11"),sQuery(id+"F0.wireOp",EDGE,"E12.bottom"),sQuery(id+"F0.wireOp",EDGE,"E12.top"),sQuery(id+"F0.wireOp",EDGE,"E12.left"),sQuery(id+"F0.wireOp",EDGE,"E13.bottom"),sQuery(id+"F0.wireOp",EDGE,"E13.top"),sQuery(id+"F0.wireOp",EDGE,"E14"),sQuery(id+"F0.wireOp",EDGE,"E15"),sQuery(id+"F0.wireOp",EDGE,"E16.bottom"),sQuery(id+"F0.wireOp",EDGE,"E16.top"),sQuery(id+"F0.wireOp",EDGE,"E16.left"),sQuery(id+"F0.wireOp",EDGE,"E17.bottom"),sQuery(id+"F0.wireOp",EDGE,"E17.top"),sQuery(id+"F0.wireOp",EDGE,"E18"),sQuery(id+"F0.wireOp",EDGE,"E19"),sQuery(id+"F0.wireOp",EDGE,"E20.bottom"),sQuery(id+"F0.wireOp",EDGE,"E20.top"),sQuery(id+"F0.wireOp",EDGE,"E20.left"),sQuery(id+"F0.wireOp",EDGE,"E21.bottom"),sQuery(id+"F0.wireOp",EDGE,"E21.top"),sQuery(id+"F0.wireOp",EDGE,"E22"),sQuery(id+"F0.wireOp",EDGE,"E23"),sQuery(id+"F0.wireOp",EDGE,"E24.bottom"),sQuery(id+"F0.wireOp",EDGE,"E24.top"),sQuery(id+"F0.wireOp",EDGE,"E24.left"),sQuery(id+"F0.wireOp",EDGE,"E25.bottom"),sQuery(id+"F0.wireOp",EDGE,"E25.top"),sQuery(id+"F0.wireOp",EDGE,"E26"),sQuery(id+"F0.wireOp",EDGE,"E27"),sQuery(id+"F0.wireOp",EDGE,"E28.bottom"),sQuery(id+"F0.wireOp",EDGE,"E28.top"),sQuery(id+"F0.wireOp",EDGE,"E28.left"),sQuery(id+"F0.wireOp",EDGE,"E29.bottom"),sQuery(id+"F0.wireOp",EDGE,"E29.top"),sQuery(id+"F0.wireOp",EDGE,"E30"),sQuery(id+"F0.wireOp",EDGE,"E31"),sQuery(id+"F0.wireOp",EDGE,"E34.bottom"),sQuery(id+"F0.wireOp",EDGE,"E34.top"),sQuery(id+"F0.wireOp",EDGE,"E34.left"),sQuery(id+"F0.wireOp",EDGE,"E35.bottom"),sQuery(id+"F0.wireOp",EDGE,"E35.top"),sQuery(id+"F0.wireOp",EDGE,"E36"),sQuery(id+"F0.wireOp",EDGE,"E37"),sQuery(id+"F0.wireOp",EDGE,"E38.bottom"),sQuery(id+"F0.wireOp",EDGE,"E38.top"),sQuery(id+"F0.wireOp",EDGE,"E38.left"),sQuery(id+"F0.wireOp",EDGE,"E39.bottom"),sQuery(id+"F0.wireOp",EDGE,"E39.top"),sQuery(id+"F0.wireOp",EDGE,"E40"),sQuery(id+"F0.wireOp",EDGE,"E41"),sQuery(id+"F0.wireOp",EDGE,"E42.bottom"),sQuery(id+"F0.wireOp",EDGE,"E42.top"),sQuery(id+"F0.wireOp",EDGE,"E42.left"),sQuery(id+"F0.wireOp",EDGE,"E43.bottom"),sQuery(id+"F0.wireOp",EDGE,"E43.top"),sQuery(id+"F0.wireOp",EDGE,"E44"),sQuery(id+"F0.wireOp",EDGE,"E45"),sQuery(id+"F0.wireOp",EDGE,"E46.bottom"),sQuery(id+"F0.wireOp",EDGE,"E46.top"),sQuery(id+"F0.wireOp",EDGE,"E46.left"),sQuery(id+"F0.wireOp",EDGE,"E47.bottom"),sQuery(id+"F0.wireOp",EDGE,"E47.top"),sQuery(id+"F0.wireOp",EDGE,"E48"),sQuery(id+"F0.wireOp",EDGE,"E49"),sQuery(id+"F0.wireOp",EDGE,"E50.bottom"),sQuery(id+"F0.wireOp",EDGE,"E50.top"),sQuery(id+"F0.wireOp",EDGE,"E50.left"),sQuery(id+"F0.wireOp",EDGE,"E51.bottom"),sQuery(id+"F0.wireOp",EDGE,"E51.top"),sQuery(id+"F0.wireOp",EDGE,"E52"),sQuery(id+"F0.wireOp",EDGE,"E53"),sQuery(id+"F0.wireOp",EDGE,"E54.bottom"),sQuery(id+"F0.wireOp",EDGE,"E54.top"),sQuery(id+"F0.wireOp",EDGE,"E54.left"),sQuery(id+"F0.wireOp",EDGE,"E55.bottom"),sQuery(id+"F0.wireOp",EDGE,"E55.top"),sQuery(id+"F0.wireOp",EDGE,"E56"),sQuery(id+"F0.wireOp",EDGE,"E57"),sQuery(id+"F0.wireOp",EDGE,"E58.bottom"),sQuery(id+"F0.wireOp",EDGE,"E58.top"),sQuery(id+"F0.wireOp",EDGE,"E58.left"),sQuery(id+"F0.wireOp",EDGE,"E59.bottom"),sQuery(id+"F0.wireOp",EDGE,"E59.top"),sQuery(id+"F0.wireOp",EDGE,"E60"),sQuery(id+"F0.wireOp",EDGE,"E61"),sQuery(id+"F0.wireOp",EDGE,"E62.bottom"),sQuery(id+"F0.wireOp",EDGE,"E62.top"),sQuery(id+"F0.wireOp",EDGE,"E62.left"),sQuery(id+"F0.wireOp",EDGE,"E63.left"),sQuery(id+"F0.wireOp",EDGE,"E64"),sQuery(id+"F0.wireOp",EDGE,"E65")])]});
            var Q1;
            Q1=qCreatedBy(makeId("Origin.pointOp"),VERTEX);
            transform(context, id + "F4", {"entities" : qUnion([Q0]), "transformType" : TransformType.SCALE_UNIFORMLY, "scale" : .5, "scalePoint" : qUnion([Q1]), "makeCopy" : false});
        }
    });
